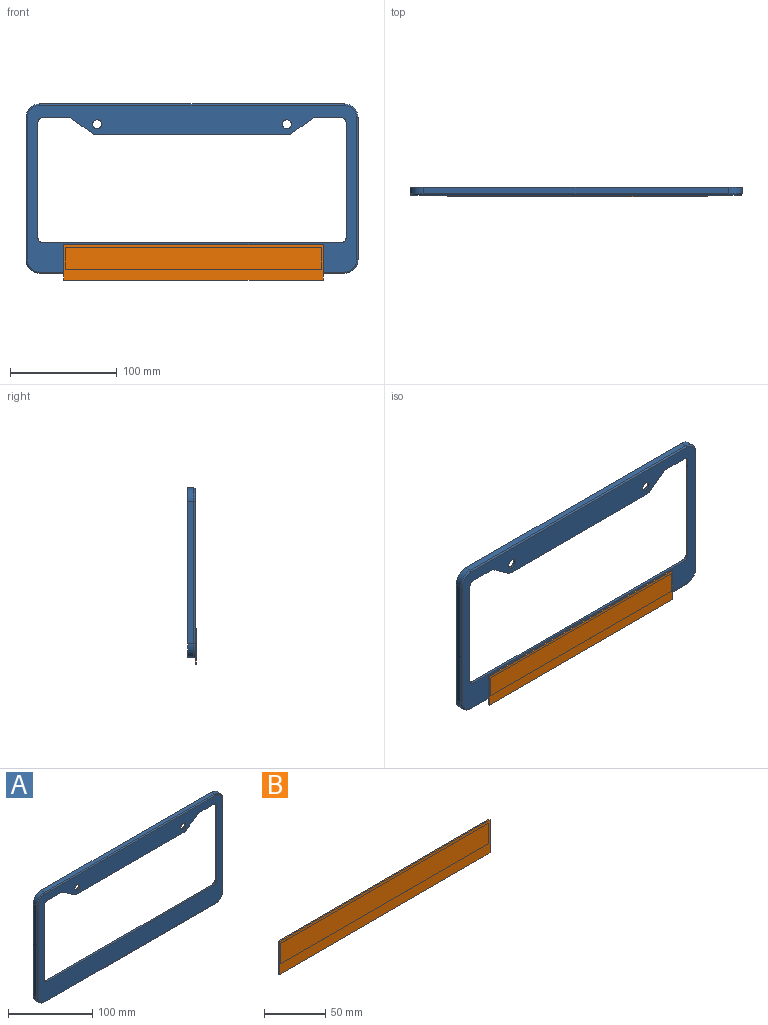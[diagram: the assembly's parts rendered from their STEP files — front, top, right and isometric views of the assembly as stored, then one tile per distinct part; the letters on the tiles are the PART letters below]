
ASSEMBLY  parts=2 mates=1
PART A: 45 faces, bbox 313.2x7.1x160.8 mm
  f0: plane 311.15x158.75mm, normal (0,1,0), area 2128mm2, adj f4,f5,f6,f7,f18,f19,f20,f21
  f1: cylinder r=6.35mm len=3.68mm, axis (0,1,0), area 9.2mm2, adj f3,f13,f14,f28
  f2: cylinder r=6.35mm len=3.68mm, axis (0,1,0), area 9.2mm2, adj f3,f14,f15,f28
  f3: plane 308.61x156.21mm, normal (0,-1,0), area 17331.2mm2, adj f1,f2,f8,f9,f10,f11,f12,f13
  f4: plane 133.35x5.84mm, normal (1,0,0), area 779mm2, adj f0,f18,f19,f43
  f5: plane 285.75x5.84mm, normal (0,0,1), area 1669.4mm2, adj f0,f18,f20,f39
  f6: plane 133.35x5.84mm, normal (-1,0,0), area 779mm2, adj f0,f20,f21,f38
  f7: plane 285.75x5.84mm, normal (0,0,-1), area 1669.4mm2, adj f0,f19,f21,f42
  f8: plane 23.31x2.34mm, normal (0,0,-1), area 54.5mm2, adj f3,f25,f26,f28
  f9: plane 107.82x2.34mm, normal (1,0,0), area 252mm2, adj f3,f24,f25,f28
  f10: plane 279.27x2.34mm, normal (0,0,1), area 652.6mm2, adj f3,f22,f24,f28
  f11: plane 107.82x2.34mm, normal (-1,0,0), area 252mm2, adj f3,f22,f23,f28
  f12: plane 23.31x2.34mm, normal (0,0,-1), area 54.5mm2, adj f3,f23,f27,f28
  f13: plane 19.06x13.53mm, normal (0.58,0,-0.82), area 54.6mm2, adj f1,f3,f27,f28
  f14: plane 179.82x2.34mm, normal (0,0,-1), area 420.2mm2, adj f1,f2,f3,f28
  f15: plane 19.06x13.53mm, normal (-0.58,0,-0.82), area 54.6mm2, adj f2,f3,f26,f28
  f16: cylinder r=4.32mm len=8.64mm, axis (0,1,0), area 63.4mm2, adj f3,f28
  f17: cylinder r=4.32mm len=8.64mm, axis (0,1,0), area 63.4mm2, adj f3,f28
  f18: cylinder r=12.7mm len=12.7mm, axis (0,1,0), area 116.5mm2, adj f0,f4,f5,f41
  f19: cylinder r=12.7mm len=12.7mm, axis (0,1,0), area 116.5mm2, adj f0,f4,f7,f44
  f20: cylinder r=12.7mm len=12.7mm, axis (0,1,0), area 116.5mm2, adj f0,f5,f6,f37
  f21: cylinder r=12.7mm len=12.7mm, axis (0,1,0), area 116.5mm2, adj f0,f6,f7,f40
  f22: cylinder r=4.83mm len=4.83mm, axis (0,-1,0), area 17.7mm2, adj f3,f10,f11,f28
  f23: cylinder r=4.83mm len=4.83mm, axis (0,-1,0), area 17.7mm2, adj f3,f11,f12,f28
  f24: cylinder r=4.83mm len=4.83mm, axis (0,-1,0), area 17.7mm2, adj f3,f9,f10,f28
  f25: cylinder r=4.83mm len=4.83mm, axis (0,-1,0), area 17.7mm2, adj f3,f8,f9,f28
  f26: cylinder r=6.35mm len=3.68mm, axis (0,-1,0), area 9.2mm2, adj f3,f8,f15,f28
  f27: cylinder r=6.35mm len=3.68mm, axis (0,-1,0), area 9.2mm2, adj f3,f12,f13,f28
  f28: plane 306.48x154.08mm, normal (0,1,0), area 16364mm2, adj f1,f2,f8,f9,f10,f11,f12,f13
  f29: plane 133.35x4.78mm, normal (-1,0,0), area 636.8mm2, adj f0,f28,f33,f34
  f30: plane 285.75x4.78mm, normal (0,0,-1), area 1364.5mm2, adj f0,f28,f33,f35
  f31: plane 133.35x4.78mm, normal (1,0,0), area 636.8mm2, adj f0,f28,f35,f36
  f32: plane 285.75x4.78mm, normal (0,0,1), area 1364.5mm2, adj f0,f28,f34,f36
  f33: cylinder r=10.36mm len=10.36mm, axis (0,1,0), area 77.7mm2, adj f0,f28,f29,f30
  f34: cylinder r=10.36mm len=10.36mm, axis (0,1,0), area 77.7mm2, adj f0,f28,f29,f32
  f35: cylinder r=10.36mm len=10.36mm, axis (0,1,0), area 77.7mm2, adj f0,f28,f30,f31
  f36: cylinder r=10.36mm len=10.36mm, axis (0,1,0), area 77.7mm2, adj f0,f28,f31,f32
  f37: torus R=11.43mm, axis (0,1,0), area 38.4mm2, adj f3,f20,f38,f39
  f38: cylinder r=1.27mm len=133.35mm, axis (0,0,-1), area 266mm2, adj f3,f6,f37,f40
  f39: cylinder r=1.27mm len=285.75mm, axis (-1,0,0), area 570mm2, adj f3,f5,f37,f41
  f40: torus R=11.43mm, axis (0,1,0), area 38.4mm2, adj f3,f21,f38,f42
  f41: torus R=11.43mm, axis (0,1,0), area 38.4mm2, adj f3,f18,f39,f43
  f42: cylinder r=1.27mm len=285.75mm, axis (1,0,0), area 570mm2, adj f3,f7,f40,f44
  f43: cylinder r=1.27mm len=133.35mm, axis (0,0,1), area 266mm2, adj f3,f4,f41,f44
  f44: torus R=11.43mm, axis (0,1,0), area 38.4mm2, adj f3,f19,f42,f43
PART B: 11 faces, bbox 243x1.2x33 mm
  f0: plane 243x33mm, normal (0,-1,0), area 3135mm2, adj f1,f2,f3,f4,f6,f7,f8,f9
  f1: plane 33x1.2mm, normal (1,0,0), area 39.6mm2, adj f0,f2,f4,f5
  f2: plane 243x1.2mm, normal (0,0,1), area 291.6mm2, adj f0,f1,f3,f5
  f3: plane 33x1.2mm, normal (-1,0,0), area 39.6mm2, adj f0,f2,f4,f5
  f4: plane 243x1.2mm, normal (0,0,-1), area 291.6mm2, adj f0,f1,f3,f5
  f5: plane 243x33mm, normal (0,1,0), area 8019mm2, adj f1,f2,f3,f4
  f6: plane 240x0.01mm, normal (0,0,-1), area 2.4mm2, adj f0,f7,f9,f10
  f7: plane 20.35x0.01mm, normal (1,0,0), area 0.2mm2, adj f0,f6,f8,f10
  f8: plane 240x0.01mm, normal (0,0,1), area 2.4mm2, adj f0,f7,f9,f10
  f9: plane 20.35x0.01mm, normal (-1,0,0), area 0.2mm2, adj f0,f6,f8,f10
  f10: plane 240x20.35mm, normal (0,-1,0), area 4884mm2, adj f6,f7,f8,f9
PLACE A at identity fixed
PLACE B t=(1.35,-7.11,-69.1)mm
MATE planar B.f5 <-> A.f3  axis (0,1,0) through (1.35,-7.11,-69.1)mm
